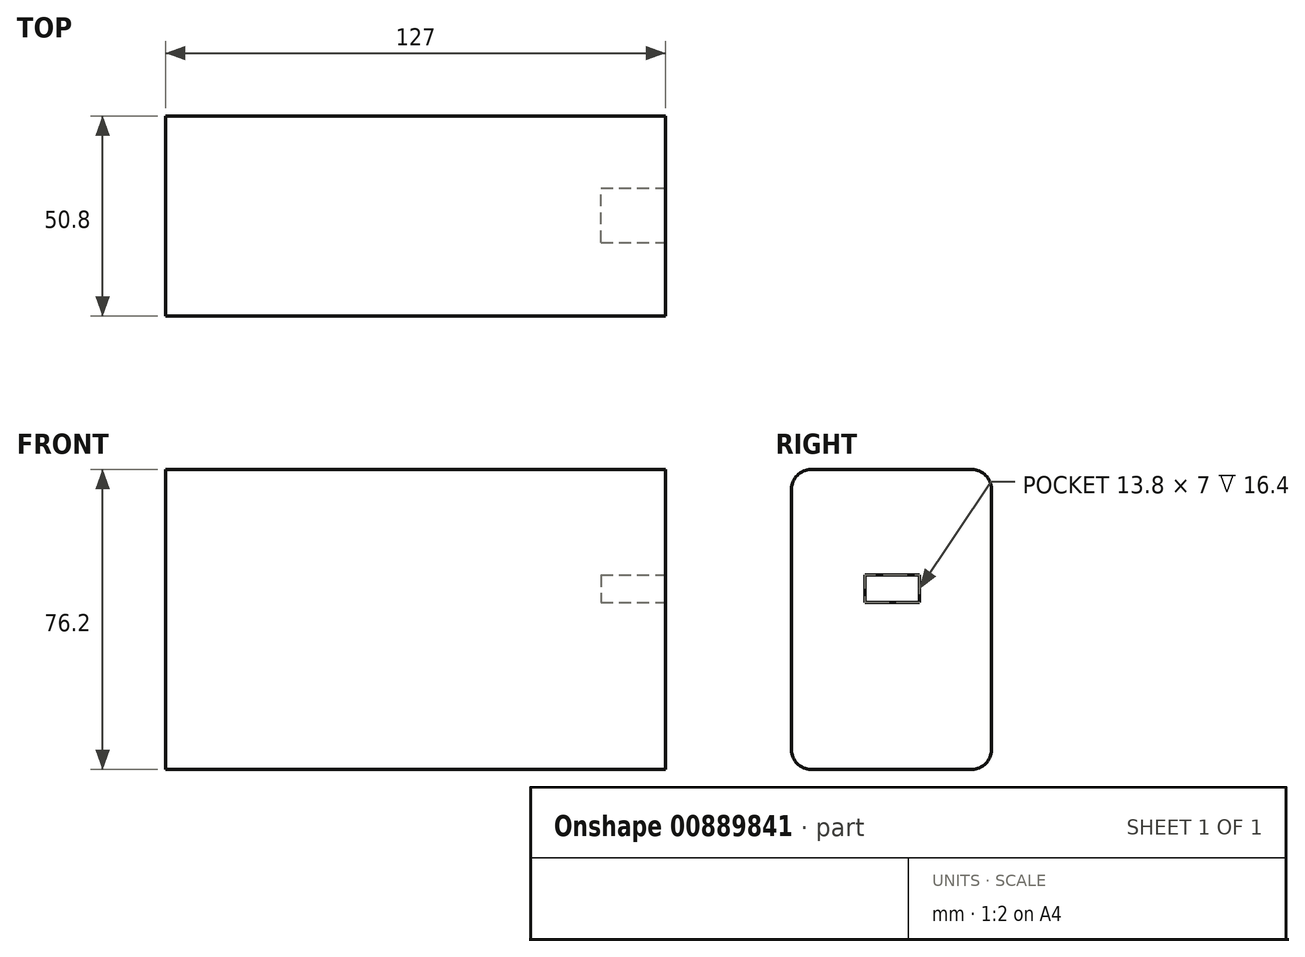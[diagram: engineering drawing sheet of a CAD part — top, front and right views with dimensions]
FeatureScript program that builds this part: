
annotation { "Feature Type Name" : "Feature", "Feature Type Description" : "" }
export const myFeature = defineFeature(function(context is Context, id is Id, definition is map)
    precondition{}
    {
        {
            var Q0;
            Q0=qCreatedBy(makeId("Front.planeOp"),FACE);
            var sketch = newSketch(context, id + "F0", { "sketchPlane" : qUnion([Q0])});
            skLineSegment(sketch, "E0.bottom", {"start": v(63.5, -38.1) * mm, "end": v(-63.5, -38.1) * mm});
            skLineSegment(sketch, "E0.top", {"start": v(63.5, 38.1) * mm, "end": v(-63.5, 38.1) * mm});
            skLineSegment(sketch, "E0.left", {"start": v(63.5, -38.1) * mm, "end": v(63.5, 38.1) * mm});
            skLineSegment(sketch, "E0.right", {"start": v(-63.5, -38.1) * mm, "end": v(-63.5, 38.1) * mm});
            skPoint(sketch, "E0.middle", {"position": v(0, 0) * mm});
            skSolve(sketch);
        }
        {
            var Q0;
            Q0 = qSketchRegion(id + "F0", true);
            extrude(context, id + "F1", {"entities" : qUnion([Q0]), "depth" : 50.8 * mm, "offsetDistance" : 25.4 * mm});
        }
        {
            var Q0;
            Q0=makeQuery(id+"F1.opExtrude","CAP_EDGE",EDGE,{"disambiguationData":[OSD([sQuery(id+"F0.wireOp",EDGE,"E0.top")])],"isStart":false});
            var Q1;
            Q1=makeQuery(id+"F1.opExtrude","CAP_EDGE",EDGE,{"disambiguationData":[OSD([sQuery(id+"F0.wireOp",EDGE,"E0.top")])],"isStart":true});
            var Q2;
            Q2=makeQuery(id+"F1.opExtrude","CAP_EDGE",EDGE,{"disambiguationData":[OSD([sQuery(id+"F0.wireOp",EDGE,"E0.bottom")])],"isStart":true});
            var Q3;
            Q3=makeQuery(id+"F1.opExtrude","CAP_EDGE",EDGE,{"disambiguationData":[OSD([sQuery(id+"F0.wireOp",EDGE,"E0.bottom")])],"isStart":false});
            fillet(context, id + "F2", {"entities" : qUnion([Q0, Q1, Q2, Q3]), "radius" : 5 * mm, "tangentPropagation" : true, "allowEdgeOverflow" : false});
        }
        {
            var Q0;
            Q0=makeQuery(id+"F1.opExtrude","SWEPT_FACE",FACE,{"disambiguationData":[OSD([sQuery(id+"F0.wireOp",EDGE,"E0.left")])]});
            var sketch = newSketch(context, id + "F3", { "sketchPlane" : qUnion([Q0])});
            skLineSegment(sketch, "E1.bottom", {"start": v(-32.08, 11.28) * mm, "end": v(-18.28, 11.28) * mm});
            skLineSegment(sketch, "E1.top", {"start": v(-32.08, 4.28) * mm, "end": v(-18.28, 4.28) * mm});
            skLineSegment(sketch, "E1.left", {"start": v(-32.08, 11.28) * mm, "end": v(-32.08, 4.28) * mm});
            skLineSegment(sketch, "E1.right", {"start": v(-18.28, 11.28) * mm, "end": v(-18.28, 4.28) * mm});
            skSolve(sketch);
        }
        {
            var Q0;
            Q0 = qSketchRegion(id + "F3", true);
            extrude(context, id + "F4", {"entities" : qUnion([Q0]), "operationType" : NewBodyOperationType.REMOVE, "oppositeDirection" : true, "depth" : 16.4 * mm, "offsetDistance" : 25.4 * mm});
        }
    });
